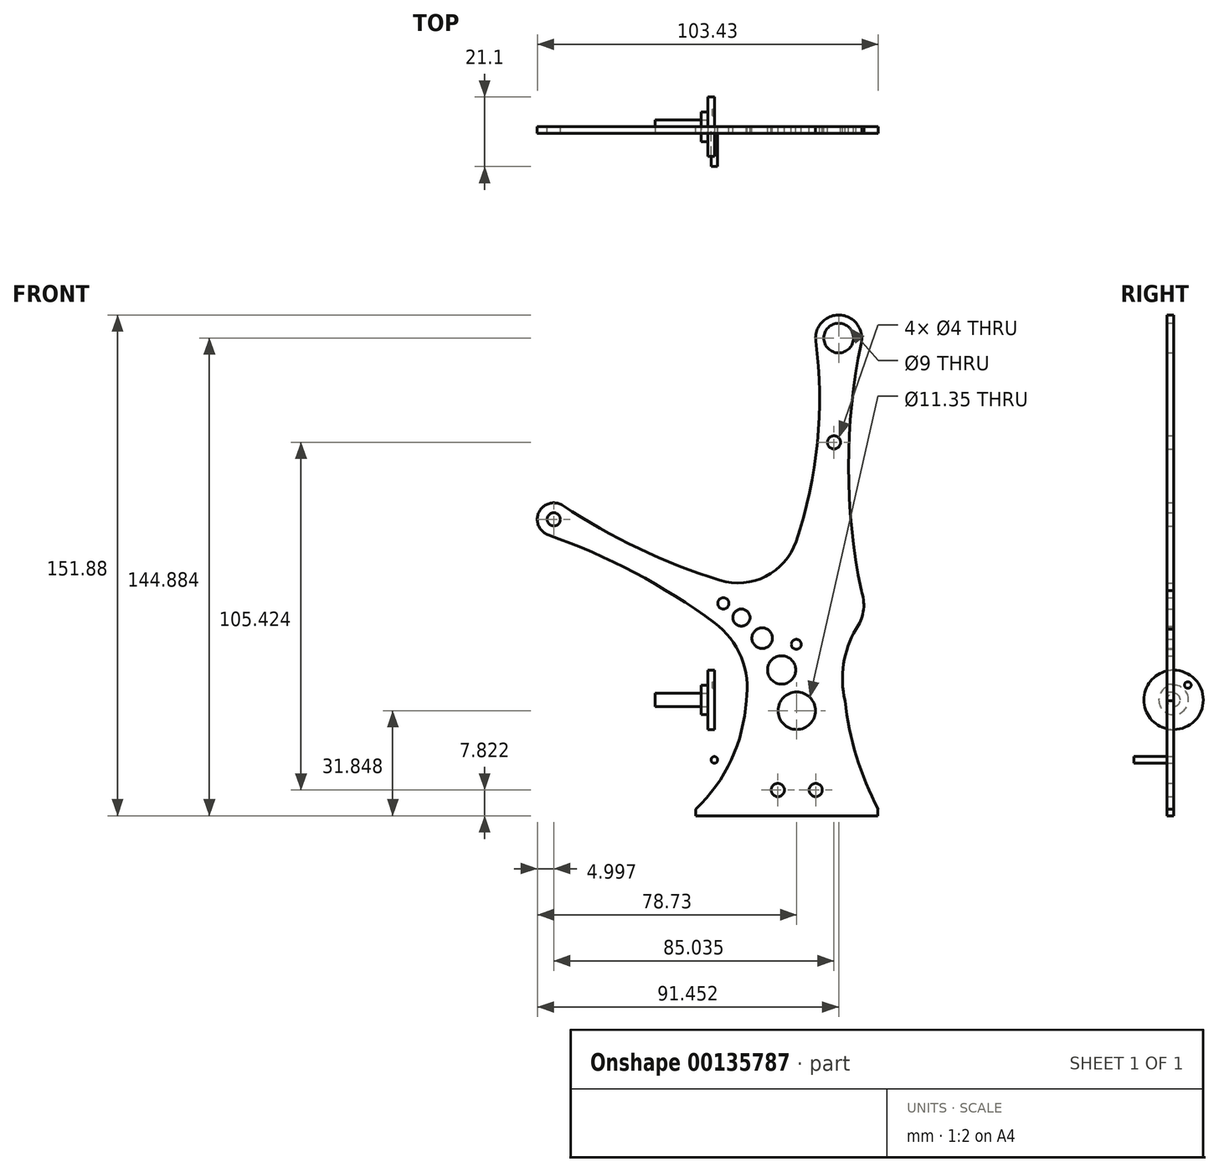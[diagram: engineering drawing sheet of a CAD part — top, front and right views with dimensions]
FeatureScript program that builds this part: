
annotation { "Feature Type Name" : "Feature", "Feature Type Description" : "" }
export const myFeature = defineFeature(function(context is Context, id is Id, definition is map)
    precondition{}
    {
        {
            var Q0;
            Q0=qCreatedBy(makeId("Front.planeOp"),FACE);
            var sketch = newSketch(context, id + "F0", { "sketchPlane" : qUnion([Q0])});
            skArc(sketch, "E0", {"start": v(9.64, 17.95) * mm, "mid": v(8.16, 31.14) * mm, "end": v(0, 41.6) * mm});
            skArc(sketch, "E1", {"start": v(-45.97, 77.1) * mm, "mid": v(-53.21, 75.16) * mm, "end": v(-50.4, 68.22) * mm});
            skArc(sketch, "E2", {"start": v(42.96, 39.66) * mm, "mid": v(39.2, 29.13) * mm, "end": v(39.64, 17.95) * mm});
            skArc(sketch, "E3", {"start": v(42.96, 39.66) * mm, "mid": v(45.18, 44.94) * mm, "end": v(44.8, 50.67) * mm});
            skArc(sketch, "E4", {"start": v(44.58, 51.37) * mm, "mid": v(44.69, 51.02) * mm, "end": v(44.8, 50.67) * mm});
            skArc(sketch, "E5", {"start": v(-45.97, 77.1) * mm, "mid": v(-22.97, 64.11) * mm, "end": v(1.63, 54.46) * mm});
            skArc(sketch, "E6", {"start": v(0, 41.6) * mm, "mid": v(-24.21, 56.77) * mm, "end": v(-50.4, 68.22) * mm});
            skArc(sketch, "E7", {"start": v(1.63, 54.46) * mm, "mid": v(15.6, 55.63) * mm, "end": v(24.78, 66.24) * mm});
            skPoint(sketch, "E8", {"position": v(39.64, 17.95) * mm});
            skLineSegment(sketch, "E9", {"start": v(49.7, 17.95) * mm, "end": v(-14.45, 17.95) * mm, "construction": true});
            skCircle(sketch, "E10", {"center": v(-48.73, 72.94) * mm, "radius": 2 * mm});
            skCircle(sketch, "E11", {"center": v(37.72, 127.92) * mm, "radius": 4.5 * mm});
            skCircle(sketch, "E12", {"center": v(19.25, -9.14) * mm, "radius": 2 * mm});
            skCircle(sketch, "E13", {"center": v(30.75, -9.14) * mm, "radius": 2 * mm});
            skLineSegment(sketch, "E14", {"start": v(10.78, -9.14) * mm, "end": v(42.85, -9.14) * mm, "construction": true});
            skLineSegment(sketch, "E15", {"start": v(25, -3.96) * mm, "end": v(25, 21.05) * mm, "construction": true});
            skCircle(sketch, "E16", {"center": v(25, 14.89) * mm, "radius": 5.68 * mm});
            skCircle(sketch, "E17", {"center": v(20.42, 27.27) * mm, "radius": 4.3 * mm});
            skCircle(sketch, "E18", {"center": v(14.52, 36.9) * mm, "radius": 3.12 * mm});
            skCircle(sketch, "E19", {"center": v(8.2, 43.13) * mm, "radius": 2.6 * mm});
            skCircle(sketch, "E20", {"center": v(2.72, 47.45) * mm, "radius": 1.71 * mm});
            skArc(sketch, "E21", {"start": v(44.58, 126.5) * mm, "mid": v(40.72, 88.94) * mm, "end": v(44.58, 51.37) * mm});
            skArc(sketch, "E22", {"start": v(24.78, 66.24) * mm, "mid": v(31.26, 96.29) * mm, "end": v(30.78, 127.02) * mm});
            skArc(sketch, "E23", {"start": v(44.58, 126.5) * mm, "mid": v(37.99, 134.92) * mm, "end": v(30.78, 127.02) * mm});
            skArc(sketch, "E24", {"start": v(-5.64, -14.96) * mm, "mid": v(5.15, 0.04) * mm, "end": v(9.64, 17.95) * mm});
            skArc(sketch, "E25", {"start": v(39.64, 17.95) * mm, "mid": v(43.1, 1.02) * mm, "end": v(49.7, -14.96) * mm});
            skLineSegment(sketch, "E26", {"start": v(-5.64, -14.96) * mm, "end": v(49.7, -14.96) * mm});
            skLineSegment(sketch, "E27.bottom", {"start": v(-5.64, -14.96) * mm, "end": v(49.55, -14.96) * mm});
            skLineSegment(sketch, "E27.top", {"start": v(-5.64, -16.96) * mm, "end": v(49.55, -16.96) * mm});
            skLineSegment(sketch, "E27.left", {"start": v(-5.64, -14.96) * mm, "end": v(-5.64, -16.96) * mm});
            skLineSegment(sketch, "E27.right", {"start": v(49.55, -14.96) * mm, "end": v(49.55, -16.96) * mm});
            skCircle(sketch, "E28", {"center": v(36.3, 96.29) * mm, "radius": 2 * mm});
            skPoint(sketch, "E28.centerSnap0", {"position": v(31.26, 96.29) * mm});
            skCircle(sketch, "E29", {"center": v(24.85, 35.04) * mm, "radius": 1.5 * mm});
            skSolve(sketch);
        }
        {
            var Q0;
            Q0 = qSketchRegion(id + "F0", true);
            extrude(context, id + "F1", {"entities" : qUnion([Q0]), "depth" : 2 * mm});
        }
        {
            var Q0;
            Q0=qCreatedBy(makeId("Front.planeOp"),FACE);
            var sketch = newSketch(context, id + "F2", { "sketchPlane" : qUnion([Q0])});
            skLineSegment(sketch, "E30", {"start": v(0, 0) * mm, "end": v(0, 9.18) * mm, "construction": true});
            skLineSegment(sketch, "E31", {"start": v(0, 9.18) * mm, "end": v(-2, 9.18) * mm});
            skLineSegment(sketch, "E32", {"start": v(-2, 9.18) * mm, "end": v(-2, 13.68) * mm});
            skLineSegment(sketch, "E33", {"start": v(-2, 13.68) * mm, "end": v(-4, 13.68) * mm});
            skLineSegment(sketch, "E34", {"start": v(-4, 13.68) * mm, "end": v(-4, 16.18) * mm});
            skLineSegment(sketch, "E35", {"start": v(-4, 16.18) * mm, "end": v(-18, 16.18) * mm});
            skLineSegment(sketch, "E36", {"start": v(-18, 16.18) * mm, "end": v(-18, 18.18) * mm});
            skLineSegment(sketch, "E37", {"start": v(-18, 18.18) * mm, "end": v(0, 18.18) * mm});
            skLineSegment(sketch, "E38", {"start": v(0, 18.18) * mm, "end": v(0, 9.18) * mm});
            skLineSegment(sketch, "E39", {"start": v(11.11, 18.18) * mm, "end": v(-47.59, 18.18) * mm, "construction": true});
            skSolve(sketch);
        }
        {
            var Q0;
            Q0=makeQuery(id+"F2.imprint","IMPRINT",FACE,{"disambiguationData":[TD([[makeQuery(id+"F2.imprint","IMPRINT",EDGE,{"derivedFrom":sQuery(id+"F2.wireOp",EDGE,"E31")}),-1.0]])]});
            var Q1;
            Q1=sQuery(id+"F2.wireOp",EDGE,"E39");
            revolve(context, id + "F3", {"entities" : qUnion([Q0]), "axis" : qUnion([Q1]), "revolveType" : RevolveType.FULL});
        }
        {
            var Q0;
            Q0=makeQuery(id+"F3.opRevolve","SWEPT_FACE",FACE,{"disambiguationData":[OSD([sQuery(id+"F2.wireOp",EDGE,"E38")])]});
            var sketch = newSketch(context, id + "F4", { "sketchPlane" : qUnion([Q0])});
            skCircle(sketch, "E40", {"center": v(4.3, 22.69) * mm, "radius": 1 * mm});
            skSolve(sketch);
        }
        {
            var Q0;
            Q0 = qSketchRegion(id + "F4", true);
            extrude(context, id + "F5", {"entities" : qUnion([Q0]), "operationType" : NewBodyOperationType.REMOVE, "oppositeDirection" : true, "depth" : .55 * mm});
        }
        {
            var Q0;
            Q0=qCreatedBy(makeId("Front.planeOp"),FACE);
            var sketch = newSketch(context, id + "F6", { "sketchPlane" : qUnion([Q0])});
            skLineSegment(sketch, "E41", {"start": v(0, 18.18) * mm, "end": v(0, 0) * mm, "construction": true});
            skLineSegment(sketch, "E42", {"start": v(11.17, 18.18) * mm, "end": v(-31.31, 18.18) * mm, "construction": true});
            skLineSegment(sketch, "E43.0", {"start": v(-18, 16.18) * mm, "end": v(-18, 18.18) * mm});
            skLineSegment(sketch, "E44.0", {"start": v(-2, 9.18) * mm, "end": v(-2, 13.68) * mm});
            skLineSegment(sketch, "E45.0", {"start": v(0, 9.18) * mm, "end": v(-2, 9.18) * mm});
            skLineSegment(sketch, "E46", {"start": v(-18, 18.18) * mm, "end": v(-18, 16.18) * mm});
            skLineSegment(sketch, "E47", {"start": v(-2, 16.18) * mm, "end": v(-2, 9.18) * mm});
            skLineSegment(sketch, "E48", {"start": v(-2, 9.18) * mm, "end": v(0, 9.18) * mm});
            skLineSegment(sketch, "E49", {"start": v(0, 18.18) * mm, "end": v(0, 9.18) * mm});
            skLineSegment(sketch, "E50", {"start": v(0, 18.18) * mm, "end": v(-18, 18.18) * mm});
            skPoint(sketch, "E51.0.end.orphan", {"position": v(-18, 16.18) * mm});
            skLineSegment(sketch, "E52", {"start": v(-18, 16.18) * mm, "end": v(-2, 16.18) * mm});
            skSolve(sketch);
        }
        {
            var Q0;
            Q0 = qSketchRegion(id + "F6", true);
            var Q1;
            Q1=sQuery(id+"F6.wireOp",EDGE,"E42");
            revolve(context, id + "F7", {"entities" : qUnion([Q0]), "axis" : qUnion([Q1]), "revolveType" : RevolveType.FULL});
        }
        {
            var Q0;
            Q0=makeQuery(id+"F4.imprint","IMPRINT",FACE,{"disambiguationData":[TD([[makeQuery(id+"F4.imprint","IMPRINT",EDGE,{"derivedFrom":sQuery(id+"F4.wireOp",EDGE,"E40")}),1.0]])]});
            extrude(context, id + "F8", {"entities" : qUnion([Q0]), "operationType" : NewBodyOperationType.REMOVE, "oppositeDirection" : true, "depth" : .55 * mm});
        }
        {
            var Q0;
            Q0=qCreatedBy(makeId("Front.planeOp"),FACE);
            var sketch = newSketch(context, id + "F9", { "sketchPlane" : qUnion([Q0])});
            skCircle(sketch, "E53", {"center": v(0, 0) * mm, "radius": 1 * mm});
            skSolve(sketch);
        }
        {
            var Q0;
            Q0 = qSketchRegion(id + "F9", true);
            extrude(context, id + "F10", {"entities" : qUnion([Q0]), "depth" : 12.1 * mm});
        }
    });
